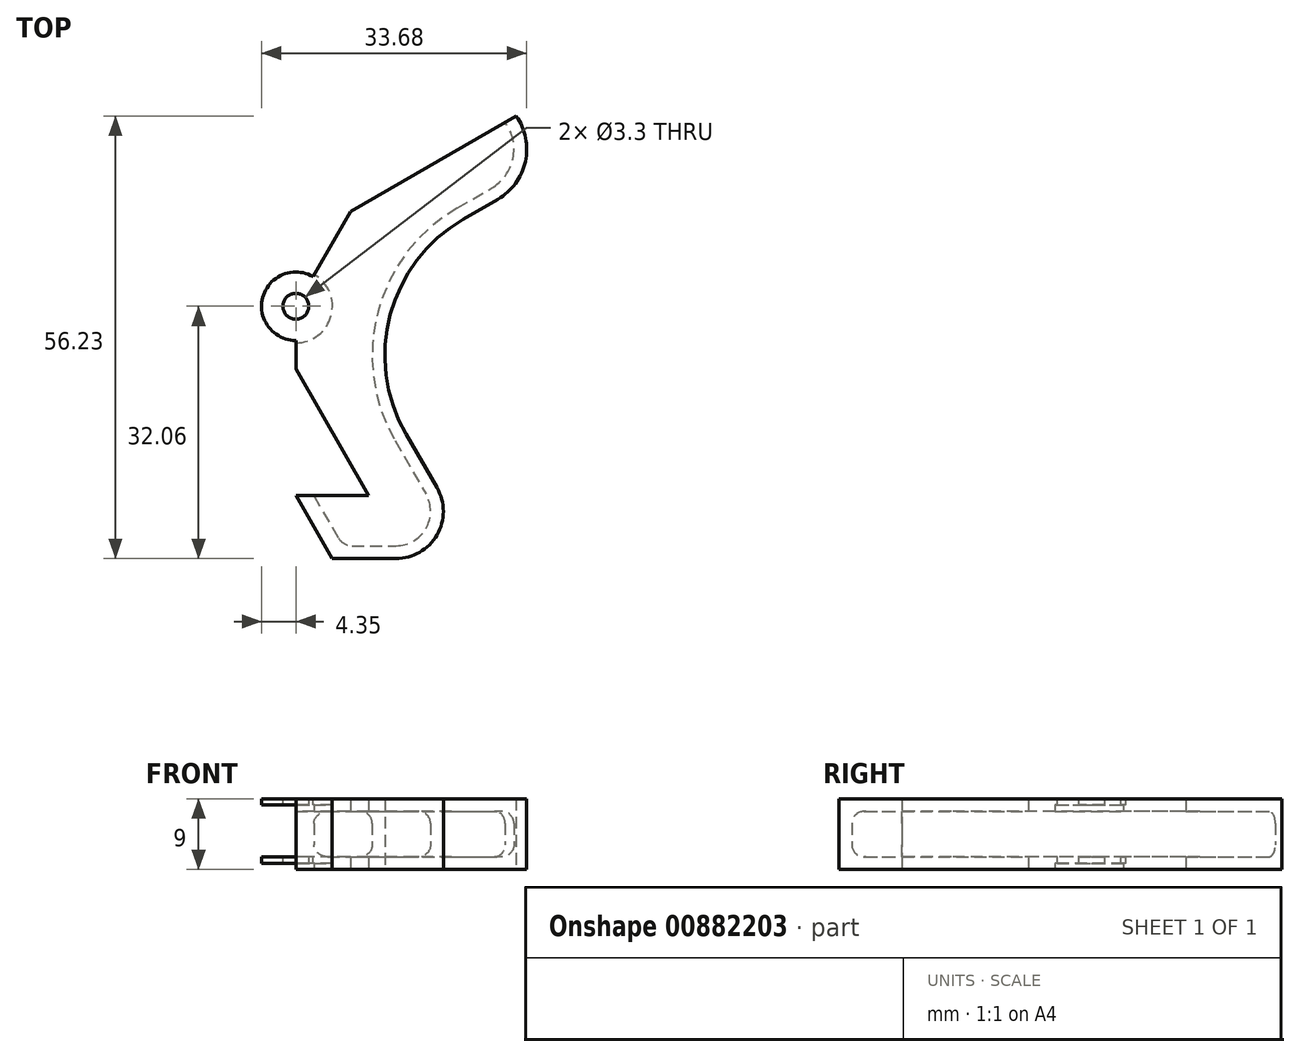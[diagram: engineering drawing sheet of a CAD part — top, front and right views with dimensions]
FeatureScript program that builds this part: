
annotation { "Feature Type Name" : "Feature", "Feature Type Description" : "" }
export const myFeature = defineFeature(function(context is Context, id is Id, definition is map)
    precondition{}
    {
        {
            var Q0;
            Q0=qCreatedBy(makeId("Top.planeOp"),FACE);
            var sketch = newSketch(context, id + "F0", { "sketchPlane" : qUnion([Q0])});
            skLineSegment(sketch, "E0", {"start": v(0, 8.75) * mm, "end": v(-8.75, -6.4) * mm});
            skLineSegment(sketch, "E1", {"start": v(-8.75, -6.4) * mm, "end": v(8.75, -6.4) * mm});
            skLineSegment(sketch, "E2", {"start": v(8.75, -6.4) * mm, "end": v(0, 8.75) * mm});
            skLineSegment(sketch, "E3.0", {"start": v(0, 9.35) * mm, "end": v(-9.27, -6.7) * mm});
            skLineSegment(sketch, "E3.1", {"start": v(9.27, -6.7) * mm, "end": v(0, 9.35) * mm});
            skLineSegment(sketch, "E3.2", {"start": v(-9.27, -6.7) * mm, "end": v(9.27, -6.7) * mm});
            skLineSegment(sketch, "E4", {"start": v(0, -6.7) * mm, "end": v(-4.62, -14.7) * mm});
            skLineSegment(sketch, "E5", {"start": v(0, -6.7) * mm, "end": v(4.62, -14.7) * mm});
            skLineSegment(sketch, "E6", {"start": v(-31.21, -14.7) * mm, "end": v(-4.62, -14.7) * mm});
            skLineSegment(sketch, "E7", {"start": v(14, 1.1) * mm, "end": v(17.93, -5.7) * mm});
            skArc(sketch, "E8.filletArc", {"start": v(12.73, -14.7) * mm, "mid": v(17.93, -11.7) * mm, "end": v(17.93, -5.7) * mm});
            skLineSegment(sketch, "E9", {"start": v(0, 9.35) * mm, "end": v(0, 15.7) * mm});
            skCircle(sketch, "E10", {"center": v(0, 17.35) * mm, "radius": 1.65 * mm});
            skLineSegment(sketch, "E11", {"start": v(-6.27, 21.73) * mm, "end": v(28, 41.52) * mm});
            skLineSegment(sketch, "E12", {"start": v(28, 41.52) * mm, "end": v(0, 41.52) * mm});
            skLineSegment(sketch, "E13", {"start": v(21.32, 28.42) * mm, "end": v(25.65, 30.92) * mm});
            skArc(sketch, "E14", {"start": v(25.65, 30.92) * mm, "mid": v(29.16, 35.7) * mm, "end": v(28, 41.52) * mm});
            skPoint(sketch, "E15.newPointA", {"position": v(0, 25.35) * mm});
            skPoint(sketch, "E15.newPointB", {"position": v(4, 18.42) * mm});
            skArc(sketch, "E15.filletArc", {"start": v(21.32, 28.42) * mm, "mid": v(12, 16.28) * mm, "end": v(14, 1.1) * mm});
            skLineSegment(sketch, "E16.trimOffspring", {"start": v(4.62, -14.7) * mm, "end": v(12.73, -14.7) * mm});
            skArc(sketch, "E17", {"start": v(-6.27, 21.73) * mm, "mid": v(-7.23, 14.85) * mm, "end": v(-2.24, 10.03) * mm});
            skLineSegment(sketch, "E18", {"start": v(0, 9.35) * mm, "end": v(-2.24, 10.03) * mm});
            skSolve(sketch);
        }
        {
            var Q0;
            {var subQ8=sQuery(id+"F0.wireOp",EDGE,"E3.1");Q0=makeQuery(id+"F0.imprint","IMPRINT",FACE,{"disambiguationData":[TD([[makeQuery(id+"F0.imprint","IMPRINT",EDGE,{"derivedFrom":subQ8}),-1.0]])]});}
            var Q1;
            {var subQ0=sQuery(id+"F0.wireOp",EDGE,"E17");Q1=makeQuery(id+"F0.imprint","IMPRINT",FACE,{"disambiguationData":[TD([[makeQuery(id+"F0.imprint","IMPRINT",EDGE,{"derivedFrom":subQ0}),1.0]])]});}
            extrude(context, id + "F1", {"entities" : qUnion([Q0, Q1]), "depth" : 9 * mm, "offsetDistance" : 25 * mm});
        }
        {
            var Q0;
            Q0=makeQuery(id+"F1.opExtrude","SWEPT_FACE",FACE,{"disambiguationData":[OSD([sQuery(id+"F0.wireOp",EDGE,"E11")])]});
            var Q1;
            Q1=makeQuery(id+"F1.opExtrude","SWEPT_FACE",FACE,{"disambiguationData":[OSD([sQuery(id+"F0.wireOp",EDGE,"E17")])]});
            var Q2;
            Q2=makeQuery(id+"F1.opExtrude","SWEPT_FACE",FACE,{"disambiguationData":[OSD([sQuery(id+"F0.wireOp",EDGE,"E3.1")])]});
            var Q3;
            Q3=makeQuery(id+"F1.opExtrude","SWEPT_FACE",FACE,{"disambiguationData":[OSD([sQuery(id+"F0.wireOp",EDGE,"E3.2")])]});
            var Q4;
            Q4=makeQuery(id+"F1.opExtrude","SWEPT_FACE",FACE,{"disambiguationData":[OSD([sQuery(id+"F0.wireOp",EDGE,"E5")])]});
            var Q5;
            Q5=makeQuery(id+"F1.opExtrude","SWEPT_FACE",FACE,{"disambiguationData":[OSD([sQuery(id+"F0.wireOp",EDGE,"E18")])]});
            shell(context, id + "F2", {"entities" : qUnion([Q0, Q1, Q2, Q3, Q4, Q5]), "thickness" : 1.62 * mm});
        }
        {
            var Q0;
            {var subQ0=sQuery(id+"F0.wireOp",EDGE,"E18");var subQ1=sQuery(id+"F0.wireOp",EDGE,"E17");var subQ2=sQuery(id+"F0.wireOp",EDGE,"E16.trimOffspring");var subQ3=sQuery(id+"F0.wireOp",EDGE,"E15.filletArc");var subQ4=sQuery(id+"F0.wireOp",EDGE,"E14");var subQ5=sQuery(id+"F0.wireOp",EDGE,"E13");var subQ6=sQuery(id+"F0.wireOp",EDGE,"E11");var subQ7=sQuery(id+"F0.wireOp",EDGE,"E10");var subQ8=sQuery(id+"F0.wireOp",EDGE,"E8.filletArc");var subQ9=sQuery(id+"F0.wireOp",EDGE,"E7");var subQ10=sQuery(id+"F0.wireOp",EDGE,"E5");var subQ11=sQuery(id+"F0.wireOp",EDGE,"E3.2");var subQ12=sQuery(id+"F0.wireOp",EDGE,"E3.1");Q0=makeQuery(id+"F2.opShell","OFFSET_FACE",FACE,{"disambiguationData":[OSD([subQ12,subQ11,subQ10,subQ9,subQ8,subQ7,subQ6,subQ5,subQ4,subQ3,subQ2,subQ1,subQ0]),TDD([makeQuery(id+"F1.opExtrude","CAP_FACE",FACE,{"disambiguationData":[OSD([subQ12,subQ11,subQ10,subQ9,subQ8,subQ7,subQ6,subQ5,subQ4,subQ3,subQ2,subQ1,subQ0])],"isStart":true})])]});}
            var sketch = newSketch(context, id + "F3", { "sketchPlane" : qUnion([Q0])});
            skCircle(sketch, "E19", {"center": v(0, 17.35) * mm, "radius": 4.65 * mm});
            skSolve(sketch);
        }
        {
            var Q0;
            Q0=qSketchRegion(id+"F3",true);
            var Q1;
            {var subQ0=sQuery(id+"F0.wireOp",EDGE,"E18");var subQ1=sQuery(id+"F0.wireOp",EDGE,"E17");var subQ2=sQuery(id+"F0.wireOp",EDGE,"E16.trimOffspring");var subQ3=sQuery(id+"F0.wireOp",EDGE,"E15.filletArc");var subQ4=sQuery(id+"F0.wireOp",EDGE,"E14");var subQ5=sQuery(id+"F0.wireOp",EDGE,"E13");var subQ6=sQuery(id+"F0.wireOp",EDGE,"E11");var subQ7=sQuery(id+"F0.wireOp",EDGE,"E10");var subQ8=sQuery(id+"F0.wireOp",EDGE,"E8.filletArc");var subQ9=sQuery(id+"F0.wireOp",EDGE,"E7");var subQ10=sQuery(id+"F0.wireOp",EDGE,"E5");var subQ11=sQuery(id+"F0.wireOp",EDGE,"E3.2");var subQ12=sQuery(id+"F0.wireOp",EDGE,"E3.1");Q1=makeQuery(id+"F2.opShell","OFFSET_FACE",FACE,{"disambiguationData":[OSD([subQ12,subQ11,subQ10,subQ9,subQ8,subQ7,subQ6,subQ5,subQ4,subQ3,subQ2,subQ1,subQ0]),TDD([makeQuery(id+"F1.opExtrude","CAP_FACE",FACE,{"disambiguationData":[OSD([subQ12,subQ11,subQ10,subQ9,subQ8,subQ7,subQ6,subQ5,subQ4,subQ3,subQ2,subQ1,subQ0])],"isStart":false})])]});}
            extrude(context, id + "F4", {"entities" : qUnion([Q0]), "operationType" : NewBodyOperationType.REMOVE, "endBound" : BoundingType.UP_TO_SURFACE, "depth" : 5 * mm, "endBoundEntityFace" : qUnion([Q1]), "offsetDistance" : 25 * mm});
        }
        {
            var Q0;
            {var subQ3=sQuery(id+"F0.wireOp",EDGE,"E3.1");Q0=makeQuery(id+"F0.imprint","IMPRINT",FACE,{"disambiguationData":[TD([[makeQuery(id+"F0.imprint","IMPRINT",EDGE,{"derivedFrom":subQ3}),-1.0]])]});}
            var sketch = newSketch(context, id + "F5", { "sketchPlane" : qUnion([Q0])});
            skLineSegment(sketch, "E20.0", {"start": v(4.62, -14.7) * mm, "end": v(12.73, -14.7) * mm});
            skLineSegment(sketch, "E21.0", {"start": v(0, -6.7) * mm, "end": v(4.62, -14.7) * mm});
            skLineSegment(sketch, "E22.0", {"start": v(0, -6.7) * mm, "end": v(9.27, -6.7) * mm});
            skPoint(sketch, "E23.orphan", {"position": v(-9.27, -6.7) * mm});
            skLineSegment(sketch, "E24", {"start": v(2.3, -6.7) * mm, "end": v(6.93, -14.7) * mm});
            skSolve(sketch);
        }
        {
            var Q0;
            {var subQ0=sQuery(id+"F5.wireOp",EDGE,"E21.0");Q0=makeQuery(id+"F5.imprint","IMPRINT",FACE,{"disambiguationData":[TD([[makeQuery(id+"F5.imprint","IMPRINT",EDGE,{"derivedFrom":subQ0}),1.0]])]});}
            extrude(context, id + "F6", {"entities" : qUnion([Q0]), "operationType" : NewBodyOperationType.ADD, "depth" : 9 * mm, "offsetDistance" : 25 * mm});
        }
        {
            var Q0;
            Q0=makeQuery(id+"F6.boolean.opBoolean","INTERSECT",EDGE,{"derivedFrom":[makeQuery(id+"F2.opShell","OFFSET_FACE",FACE,{"disambiguationData":[OSD([sQuery(id+"F0.wireOp",EDGE,"E16.trimOffspring")])]}),makeQuery(id+"F6.opExtrude","SWEPT_FACE",FACE,{"disambiguationData":[OSD([sQuery(id+"F5.wireOp",EDGE,"E24")])]})]});
            var Q1;
            Q1=makeQuery(id+"F4.boolean.opBoolean","INTERSECT",EDGE,{"disambiguationData":[OD(0.0)],"derivedFrom":[makeQuery(id+"F2.opShell","OFFSET_FACE",FACE,{"disambiguationData":[OSD([sQuery(id+"F0.wireOp",EDGE,"E15.filletArc")])]}),makeQuery(id+"F4.opExtrude","SWEPT_FACE",FACE,{"disambiguationData":[OSD([sQuery(id+"F3.wireOp",EDGE,"E19")])]})]});
            var Q2;
            Q2=makeQuery(id+"F4.boolean.opBoolean","INTERSECT",EDGE,{"disambiguationData":[OD(1.0)],"derivedFrom":[makeQuery(id+"F2.opShell","OFFSET_FACE",FACE,{"disambiguationData":[OSD([sQuery(id+"F0.wireOp",EDGE,"E15.filletArc")])]}),makeQuery(id+"F4.opExtrude","SWEPT_FACE",FACE,{"disambiguationData":[OSD([sQuery(id+"F3.wireOp",EDGE,"E19")])]})]});
            fillet(context, id + "F7", {"entities" : qUnion([Q0, Q1, Q2]), "tangentPropagation" : true, "radius" : 2 * mm, "defaultsChanged" : true, "vertexSettings" : [], "allowEdgeOverflow" : false});
        }
        {
            var Q0;
            {var subQ0=sQuery(id+"F0.wireOp",EDGE,"E7");Q0=makeQuery(id+"F2.opShell","OFFSET_EDGE",EDGE,{"disambiguationData":[OSD([subQ0]),TDD([makeQuery(id+"F1.opExtrude","CAP_EDGE",EDGE,{"disambiguationData":[OSD([subQ0])],"isStart":false})])]});}
            fillet(context, id + "F8", {"entities" : qUnion([Q0]), "tangentPropagation" : true, "radius" : 1.5 * mm, "defaultsChanged" : true, "vertexSettings" : [], "allowEdgeOverflow" : false});
        }
        {
            var Q0;
            {var subQ0=sQuery(id+"F0.wireOp",EDGE,"E15.filletArc");Q0=makeQuery(id+"F2.opShell","OFFSET_EDGE",EDGE,{"disambiguationData":[OSD([subQ0]),TDD([makeQuery(id+"F1.opExtrude","CAP_EDGE",EDGE,{"disambiguationData":[OSD([subQ0])],"isStart":true})])]});}
            fillet(context, id + "F9", {"entities" : qUnion([Q0]), "tangentPropagation" : true, "radius" : 1.5 * mm, "defaultsChanged" : true, "vertexSettings" : [], "allowEdgeOverflow" : false});
        }
        {
            var Q0;
            Q0=makeQuery(id+"F1.opExtrude","CAP_FACE",FACE,{"disambiguationData":[OSD([sQuery(id+"F0.wireOp",EDGE,"E3.1"),sQuery(id+"F0.wireOp",EDGE,"E3.2"),sQuery(id+"F0.wireOp",EDGE,"E5"),sQuery(id+"F0.wireOp",EDGE,"E7"),sQuery(id+"F0.wireOp",EDGE,"E8.filletArc"),sQuery(id+"F0.wireOp",EDGE,"E10"),sQuery(id+"F0.wireOp",EDGE,"E11"),sQuery(id+"F0.wireOp",EDGE,"E14"),sQuery(id+"F0.wireOp",EDGE,"E15.filletArc"),sQuery(id+"F0.wireOp",EDGE,"E16.trimOffspring"),sQuery(id+"F0.wireOp",EDGE,"E17"),sQuery(id+"F0.wireOp",EDGE,"E18")])],"isStart":true});
            var sketch = newSketch(context, id + "F10", { "sketchPlane" : qUnion([Q0])});
            skArc(sketch, "E25", {"start": v(0, -12.7) * mm, "mid": v(-4.65, -17.35) * mm, "end": v(0, -22) * mm});
            skLineSegment(sketch, "E26", {"start": v(0, -25.35) * mm, "end": v(0, -22) * mm});
            skLineSegment(sketch, "E27", {"start": v(0, -9.35) * mm, "end": v(0, -12.7) * mm});
            skArc(sketch, "E28.0", {"start": v(-6.27, -21.73) * mm, "mid": v(-7.23, -14.85) * mm, "end": v(-2.24, -10.03) * mm});
            skLineSegment(sketch, "E29.0", {"start": v(-6.27, -21.73) * mm, "end": v(0, -25.35) * mm});
            skLineSegment(sketch, "E30.0", {"start": v(0, -9.35) * mm, "end": v(-2.24, -10.03) * mm});
            skPoint(sketch, "E31.orphan", {"position": v(28, -41.52) * mm});
            skPoint(sketch, "E32.orphan", {"position": v(0, -26.2) * mm});
            skPoint(sketch, "E33.orphan", {"position": v(0, -7.67) * mm});
            skSolve(sketch);
        }
        {
            var Q0;
            Q0=qSketchRegion(id+"F10",true);
            extrude(context, id + "F11", {"entities" : qUnion([Q0]), "operationType" : NewBodyOperationType.REMOVE, "oppositeDirection" : true, "depth" : 25 * mm, "offsetDistance" : 25 * mm});
        }
        {
            var Q0;
            Q0=makeQuery(id+"F1.opExtrude","CAP_FACE",FACE,{"disambiguationData":[OSD([sQuery(id+"F0.wireOp",EDGE,"E3.1"),sQuery(id+"F0.wireOp",EDGE,"E3.2"),sQuery(id+"F0.wireOp",EDGE,"E5"),sQuery(id+"F0.wireOp",EDGE,"E7"),sQuery(id+"F0.wireOp",EDGE,"E8.filletArc"),sQuery(id+"F0.wireOp",EDGE,"E10"),sQuery(id+"F0.wireOp",EDGE,"E11"),sQuery(id+"F0.wireOp",EDGE,"E14"),sQuery(id+"F0.wireOp",EDGE,"E15.filletArc"),sQuery(id+"F0.wireOp",EDGE,"E16.trimOffspring"),sQuery(id+"F0.wireOp",EDGE,"E17"),sQuery(id+"F0.wireOp",EDGE,"E18")])],"isStart":true});
            var sketch = newSketch(context, id + "F12", { "sketchPlane" : qUnion([Q0])});
            skCircle(sketch, "E34", {"center": v(0, -17.35) * mm, "radius": 4.65 * mm});
            skCircle(sketch, "E35", {"center": v(0, -17.35) * mm, "radius": 1.65 * mm});
            skSolve(sketch);
        }
        {
            var Q0;
            Q0=makeQuery(id+"F12.imprint","IMPRINT",FACE,{"disambiguationData":[TD([[makeQuery(id+"F12.imprint","IMPRINT",EDGE,{"derivedFrom":sQuery(id+"F12.wireOp",EDGE,"E35")}),1.0]])]});
            extrude(context, id + "F13", {"entities" : qUnion([Q0]), "operationType" : NewBodyOperationType.REMOVE, "oppositeDirection" : true, "depth" : 0.81 * mm, "offsetDistance" : 25 * mm});
        }
        {
            var Q0;
            {var subQ0=sQuery(id+"F0.wireOp",EDGE,"E18");var subQ1=sQuery(id+"F0.wireOp",EDGE,"E17");var subQ2=sQuery(id+"F0.wireOp",EDGE,"E16.trimOffspring");var subQ3=sQuery(id+"F0.wireOp",EDGE,"E15.filletArc");var subQ4=sQuery(id+"F0.wireOp",EDGE,"E14");var subQ5=sQuery(id+"F0.wireOp",EDGE,"E11");var subQ6=sQuery(id+"F0.wireOp",EDGE,"E10");var subQ7=sQuery(id+"F0.wireOp",EDGE,"E8.filletArc");var subQ8=sQuery(id+"F0.wireOp",EDGE,"E7");var subQ9=sQuery(id+"F0.wireOp",EDGE,"E5");var subQ10=sQuery(id+"F0.wireOp",EDGE,"E3.2");var subQ11=sQuery(id+"F0.wireOp",EDGE,"E3.1");Q0=makeQuery(id+"F4.boolean.opBoolean","MERGE",FACE,{"derivedFrom":[makeQuery(id+"F2.opShell","OFFSET_FACE",FACE,{"disambiguationData":[OSD([subQ11,subQ10,subQ9,subQ8,subQ7,subQ6,subQ5,subQ4,subQ3,subQ2,subQ1,subQ0]),TDD([makeQuery(id+"F1.opExtrude","CAP_FACE",FACE,{"disambiguationData":[OSD([subQ11,subQ10,subQ9,subQ8,subQ7,subQ6,subQ5,subQ4,subQ3,subQ2,subQ1,subQ0])],"isStart":false})])]})],"fromTools":[makeQuery(id+"F4.opExtrude","CAP_FACE",FACE,{"disambiguationData":[OSD([sQuery(id+"F3.wireOp",EDGE,"E19")])],"isStart":false})]});}
            var sketch = newSketch(context, id + "F14", { "sketchPlane" : qUnion([Q0])});
            skCircle(sketch, "E36", {"center": v(0, -17.35) * mm, "radius": 1.65 * mm});
            skCircle(sketch, "E37", {"center": v(0, -17.35) * mm, "radius": 4.65 * mm});
            skSolve(sketch);
        }
        {
            var Q0;
            Q0=qSketchRegion(id+"F14",true);
            extrude(context, id + "F15", {"entities" : qUnion([Q0]), "operationType" : NewBodyOperationType.REMOVE, "oppositeDirection" : true, "depth" : 0.81 * mm, "offsetDistance" : 25 * mm});
        }
        {
            var Q0;
            Q0=makeQuery(id+"F1.opExtrude","CAP_FACE",FACE,{"disambiguationData":[OSD([sQuery(id+"F0.wireOp",EDGE,"E3.1"),sQuery(id+"F0.wireOp",EDGE,"E3.2"),sQuery(id+"F0.wireOp",EDGE,"E5"),sQuery(id+"F0.wireOp",EDGE,"E7"),sQuery(id+"F0.wireOp",EDGE,"E8.filletArc"),sQuery(id+"F0.wireOp",EDGE,"E10"),sQuery(id+"F0.wireOp",EDGE,"E11"),sQuery(id+"F0.wireOp",EDGE,"E14"),sQuery(id+"F0.wireOp",EDGE,"E15.filletArc"),sQuery(id+"F0.wireOp",EDGE,"E16.trimOffspring"),sQuery(id+"F0.wireOp",EDGE,"E17"),sQuery(id+"F0.wireOp",EDGE,"E18")])],"isStart":true});
            var sketch = newSketch(context, id + "F16", { "sketchPlane" : qUnion([Q0])});
            skLineSegment(sketch, "E38", {"start": v(2.32, -21.38) * mm, "end": v(6.93, -29.35) * mm});
            skLineSegment(sketch, "E39.0", {"start": v(0, -25.35) * mm, "end": v(6.93, -29.35) * mm});
            skLineSegment(sketch, "E40.0", {"start": v(0, -25.35) * mm, "end": v(0, -22) * mm});
            skArc(sketch, "E41.0", {"start": v(0, -22) * mm, "mid": v(1.2, -21.84) * mm, "end": v(2.32, -21.38) * mm});
            skPoint(sketch, "E42.orphan", {"position": v(0, -12.7) * mm});
            skPoint(sketch, "E43.orphan", {"position": v(28, -41.52) * mm});
            skSolve(sketch);
        }
        {
            var Q0;
            Q0=qSketchRegion(id+"F16",true);
            extrude(context, id + "F17", {"entities" : qUnion([Q0]), "operationType" : NewBodyOperationType.REMOVE, "oppositeDirection" : true, "depth" : 25 * mm, "offsetDistance" : 25 * mm});
        }
        {
            var Q0;
            Q0=makeQuery(id+"F1.opExtrude","CAP_FACE",FACE,{"disambiguationData":[OSD([sQuery(id+"F0.wireOp",EDGE,"E3.1"),sQuery(id+"F0.wireOp",EDGE,"E3.2"),sQuery(id+"F0.wireOp",EDGE,"E5"),sQuery(id+"F0.wireOp",EDGE,"E7"),sQuery(id+"F0.wireOp",EDGE,"E8.filletArc"),sQuery(id+"F0.wireOp",EDGE,"E10"),sQuery(id+"F0.wireOp",EDGE,"E11"),sQuery(id+"F0.wireOp",EDGE,"E13"),sQuery(id+"F0.wireOp",EDGE,"E14"),sQuery(id+"F0.wireOp",EDGE,"E15.filletArc"),sQuery(id+"F0.wireOp",EDGE,"E16.trimOffspring"),sQuery(id+"F0.wireOp",EDGE,"E17"),sQuery(id+"F0.wireOp",EDGE,"E18")])],"isStart":false});
            var sketch = newSketch(context, id + "F18", { "sketchPlane" : qUnion([Q0])});
            skArc(sketch, "E44.0", {"start": v(2.32, 21.38) * mm, "mid": v(-4.5, 18.55) * mm, "end": v(0, 12.7) * mm});
            skArc(sketch, "E45.0", {"start": v(2.17, 21.12) * mm, "mid": v(-4.2, 18.48) * mm, "end": v(0, 13) * mm});
            skLineSegment(sketch, "E46", {"start": v(2.17, 21.12) * mm, "end": v(2.32, 21.38) * mm});
            skLineSegment(sketch, "E47", {"start": v(0, 12.7) * mm, "end": v(0, 13) * mm});
            skSolve(sketch);
        }
        {
            var Q0;
            Q0=qSketchRegion(id+"F18",true);
            extrude(context, id + "F19", {"entities" : qUnion([Q0]), "operationType" : NewBodyOperationType.REMOVE, "oppositeDirection" : true, "depth" : 25 * mm, "offsetDistance" : 25 * mm});
        }
    });
